# Revit family: Haworth_Executive_Credenza
name_source: partatom
category: Furniture Systems
revit_build: Autodesk Revit 2018 (Build: 20170223_1515(x64)
units: mm (PartAtom-declared; Revit-internal decimal feet)

## family parameters
Always vertical = Yes
Cut with Voids When Loaded = No
OmniClass Number = 23.40.70.14.64.21
OmniClass Title = Systems Furniture
Part Type = Normal
Room Calculation Point = No
Round Connector Dimension = Use Diameter
Shared = No
Work Plane-Based = No

## types (1)
- 22d 72w
    Actual Depth = 22"
    Actual Height = 36"
    Actual Width = 72"
    Assembly Code = E2020200
    Description = Haworth - Executive Credenza
    Door Finish = Haworth _ Wood _ White Oak
    Door Offset = 1/16"
    Door Spacing = 18"
    Manufacturer = Haworth
    Model = Haworth - Executive Credenza
    Revision Number = 2
    Size = Verify Final Dim. w/ Haworth
    Standard Depth = 22 in.
    Standard Width = 72 in.
    Support Finish = Haworth _ Wood _ White Oak
    Support Thickness = 1 1/4"
    Sustainability Info = http://www.haworth.com
    Top Edge Finish = Haworth _ Wood _ White Oak
    Top Finish = Haworth _ Wood _ White Oak
    Top Thickness = 1 1/2"
    URL = http://haworth.com
    URL - Product = http://www.haworth.com
    Warranty = http://www.haworth.com

## geometry (parser evidence)
native form markers: Sweep x2
no freeform markers — native parametric forms only
